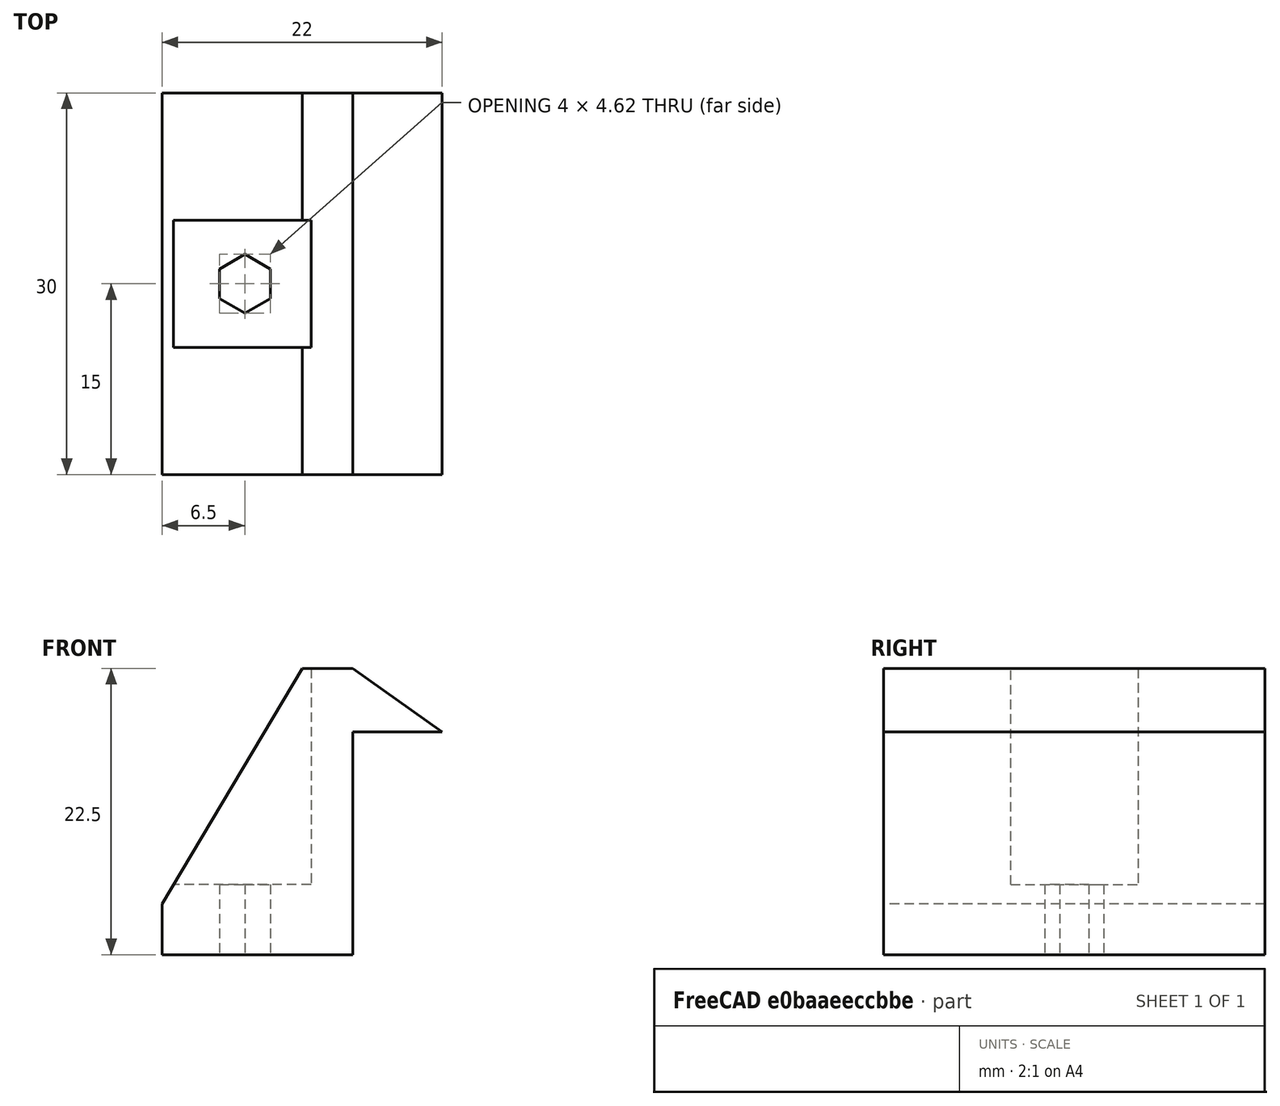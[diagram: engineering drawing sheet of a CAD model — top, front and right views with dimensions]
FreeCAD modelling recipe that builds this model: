
FCSTD DOCUMENT  (FreeCAD 0.19R)
Label: TenergyClip
License: All rights reserved
LicenseURL: http://en.wikipedia.org/wiki/All_rights_reserved
objects: Sketcher::SketchObject×4, PartDesign::Pocket×2, PartDesign::Pad×1, PartDesign::Body×1, Mesh::Feature×1
note: 11 computed .brp shape members not serialized (recipe doc carries the construction recipe); baked Part::Feature solids carry a one-line shape summary decoded from their .brp

FEATURE [Sketcher::SketchObject] Sketch
  FullyConstrained = true
  MapMode = 5
  Placement = pos=(0,0,0) rot=(1,0,0;1.5708rad)
  Support = -> [XZ_Plane]
FEATURE [Sketcher::SketchObject] Sketch001
  FullyConstrained = true
  MapMode = 5
  Placement = pos=(0,0,0) rot=(1,0,0;1.5708rad)
  Support = -> [XZ_Plane]
  sketch-geometry (7):
    g0: LineSegment StartX=0 StartY=0 StartZ=0 EndX=0 EndY=17.5 EndZ=0
    g1: LineSegment StartX=0 StartY=17.5 StartZ=0 EndX=7 EndY=17.5 EndZ=0
    g2: LineSegment StartX=7 StartY=17.5 StartZ=0 EndX=0 EndY=22.5 EndZ=0
    g3: LineSegment StartX=0 StartY=22.5 StartZ=0 EndX=-4 EndY=22.5 EndZ=0
    g4: LineSegment StartX=-4 StartY=22.5 StartZ=0 EndX=-15 EndY=4 EndZ=0
    g5: LineSegment StartX=-15 StartY=4 StartZ=0 EndX=-15 EndY=0 EndZ=0
    g6: LineSegment StartX=-15 StartY=0 StartZ=0 EndX=0 EndY=0 EndZ=0
  constraints (20):
    c: Coincident(g-1,g0)
    c: PointOnObject(g0,g-2)
    c: Coincident(g0,g1)
    c: Horizontal(g1)
    c: Coincident(g1,g2)
    c: Coincident(g2,g3)
    c: Coincident(g3,g4)
    c: PointOnObject(g5,g-1)
    c: Coincident(g5,g6)
    c: Coincident(g6,g0)
    c: Distance(g1) = 7
    c: Horizontal(g3)
    c: PointOnObject(g2,g-2)
    c: Distance(g3) = 4
    c: Vertical(g5)
    c: Distance(g5) = 4
    c: Distance(g0,g2) = 5
    c: DistanceY(g0) = 17.5
    c: Coincident(g4,g5)
    c: DistanceX(g5) = -15
FEATURE [PartDesign::Pad] Pad
  Direction = (1,1,1)
  Length = 30
  Length2 = 100
  Placement = pos=(0,0,0) rot=(1,0,0;1.5708rad)
  Profile = -> Sketch001
  Type = 0
FEATURE [Sketcher::SketchObject] Sketch005
  FullyConstrained = false
  MapMode = 5
  Placement = pos=(0,1.5e-14,22.5) rot=(0,0,1;3.14159rad)
  Support = -> [Pad]
  sketch-geometry (4):
    g0: LineSegment StartX=3.29688 StartY=20 StartZ=0 EndX=14.6344 EndY=20 EndZ=0
    g1: LineSegment StartX=14.6344 StartY=20 StartZ=0 EndX=14.6344 EndY=10 EndZ=0
    g2: LineSegment StartX=14.6344 StartY=10 StartZ=0 EndX=3.29688 EndY=10 EndZ=0
    g3: LineSegment StartX=3.29688 StartY=10 StartZ=0 EndX=3.29688 EndY=20 EndZ=0
  constraints (10):
    c: Coincident(g0,g1)
    c: Coincident(g1,g2)
    c: Coincident(g2,g3)
    c: Coincident(g3,g0)
    c: Horizontal(g0)
    c: Horizontal(g2)
    c: Vertical(g1)
    c: Vertical(g3)
    c: DistanceY(g0) = 20
    c: DistanceY(g1) = 10
FEATURE [PartDesign::Pocket] Pocket
  BaseFeature = -> Pad
  Length = 17
  Length2 = 100
  Placement = pos=(0,0,0) rot=(1,0,0;1.5708rad)
  Profile = -> Sketch005
  Type = 0
FEATURE [Sketcher::SketchObject] Sketch002
  FullyConstrained = true
  MapMode = 5
  Placement = pos=(0,6.4e-15,5.5) rot=(0,0,1;3.14159rad)
  Support = -> [Pocket]
  sketch-geometry (7):
    g0: LineSegment StartX=10.5 StartY=13.8453 StartZ=0 EndX=10.5 EndY=16.1547 EndZ=0
    g1: LineSegment StartX=10.5 StartY=16.1547 StartZ=0 EndX=8.5 EndY=17.3094 EndZ=0
    g2: LineSegment StartX=8.5 StartY=17.3094 StartZ=0 EndX=6.5 EndY=16.1547 EndZ=0
    g3: LineSegment StartX=6.5 StartY=16.1547 StartZ=0 EndX=6.5 EndY=13.8453 EndZ=0
    g4: LineSegment StartX=6.5 StartY=13.8453 StartZ=0 EndX=8.5 EndY=12.6906 EndZ=0
    g5: LineSegment StartX=8.5 StartY=12.6906 StartZ=0 EndX=10.5 EndY=13.8453 EndZ=0
    g6: Circle CenterX=8.5 CenterY=15 CenterZ=0 NormalX=0 NormalY=0 NormalZ=1 AngleXU=0 Radius=2.3094
  constraints (17):
    c: Coincident(g0,g1)
    c: Coincident(g1,g2)
    c: Coincident(g2,g3)
    c: Coincident(g3,g4)
    c: Coincident(g4,g5)
    c: Coincident(g5,g0)
    c: Equal(g0, g1-g5) x5
    c: PointOnObject(g0,g6)
    c: PointOnObject(g1,g6)
    c: PointOnObject(g2,g6)
    c: PointOnObject(g3,g6)
    c: PointOnObject(g4,g6)
    c: PointOnObject(g5,g6)
    c: Distance(g3,g1) = 4
    c: DistanceY(g6) = 15
    c: DistanceX(g6) = 8.5
    c: Vertical(g3)
FEATURE [PartDesign::Pocket] Pocket001
  BaseFeature = -> Pocket
  Length = 5
  Length2 = 100
  Placement = pos=(0,0,0) rot=(1,0,0;1.5708rad)
  Profile = -> Sketch002
  Type = 1
FEATURE [PartDesign::Body] Body
  Group = -> [Sketch,Sketch001,Pad,Sketch002,Sketch005,Pocket,Pocket001]
  Origin = -> Origin
  Tip = -> Pocket001
FEATURE [Mesh::Feature] Mesh  label="Pocket001 (Meshed)"
